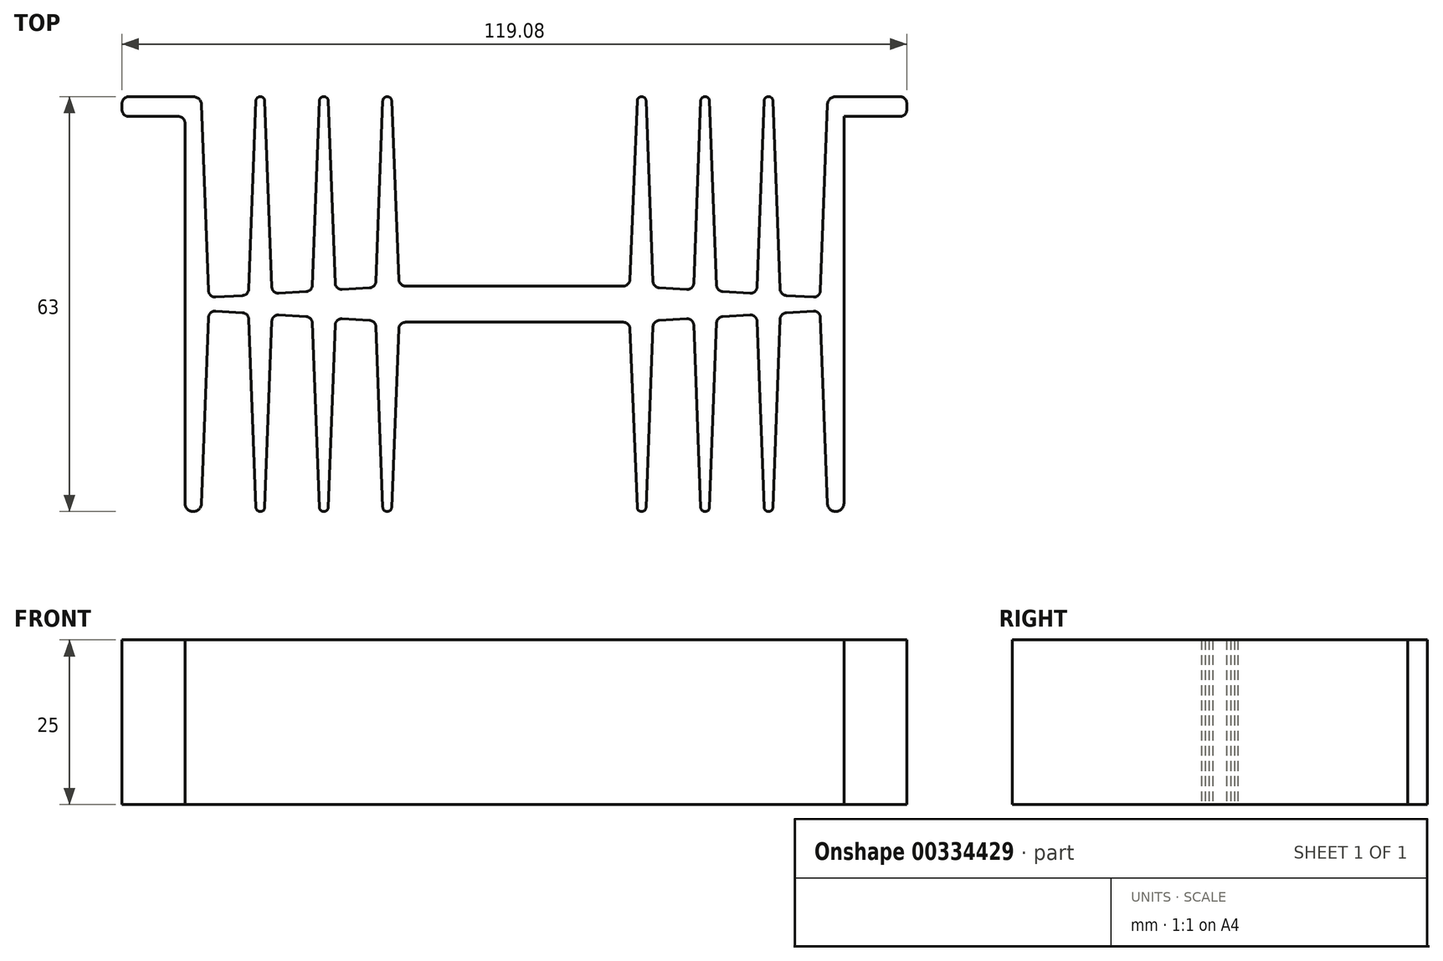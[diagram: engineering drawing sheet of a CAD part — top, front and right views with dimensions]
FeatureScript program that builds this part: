
annotation { "Feature Type Name" : "Feature", "Feature Type Description" : "" }
export const myFeature = defineFeature(function(context is Context, id is Id, definition is map)
    precondition{}
    {
        {
            var Q0;
            Q0=qCreatedBy(makeId("Top.planeOp"),FACE);
            var sketch = newSketch(context, id + "F0", { "sketchPlane" : qUnion([Q0])});
            skLineSegment(sketch, "E0.bottom", {"start": v(-50, 31.5) * mm, "end": v(50, 31.5) * mm, "construction": true});
            skLineSegment(sketch, "E0.top", {"start": v(-50, -31.5) * mm, "end": v(50, -31.5) * mm, "construction": true});
            skLineSegment(sketch, "E0.left", {"start": v(-50, 31.5) * mm, "end": v(-50, -31.5) * mm, "construction": true});
            skLineSegment(sketch, "E0.right", {"start": v(50, 31.5) * mm, "end": v(50, -31.5) * mm, "construction": true});
            skPoint(sketch, "E0.middle", {"position": v(0, 0) * mm});
            skLineSegment(sketch, "E1", {"start": v(-50, 31.5) * mm, "end": v(-47.54, 31.5) * mm});
            skLineSegment(sketch, "E2", {"start": v(-47.54, 31.5) * mm, "end": v(-46.39, 1) * mm});
            skLineSegment(sketch, "E3", {"start": v(-46.39, 1) * mm, "end": v(-40.37, 1) * mm});
            skLineSegment(sketch, "E4", {"start": v(-40.37, 1) * mm, "end": v(-39.21, 31.5) * mm});
            skLineSegment(sketch, "E5", {"start": v(-39.21, 31.5) * mm, "end": v(-37.91, 31.5) * mm});
            skLineSegment(sketch, "E6", {"start": v(-37.91, 31.5) * mm, "end": v(-36.76, 1) * mm});
            skLineSegment(sketch, "E7", {"start": v(-36.76, 1) * mm, "end": v(-30.74, 1) * mm});
            skLineSegment(sketch, "E8", {"start": v(-30.74, 1) * mm, "end": v(-29.59, 31.5) * mm});
            skLineSegment(sketch, "E9", {"start": v(-29.59, 31.5) * mm, "end": v(-28.29, 31.5) * mm});
            skLineSegment(sketch, "E10", {"start": v(-28.29, 31.5) * mm, "end": v(-27.13, 1) * mm});
            skLineSegment(sketch, "E11", {"start": v(-27.13, 1) * mm, "end": v(-21.11, 1) * mm});
            skLineSegment(sketch, "E12", {"start": v(-21.11, 1) * mm, "end": v(-19.96, 31.5) * mm});
            skLineSegment(sketch, "E13", {"start": v(-19.96, 31.5) * mm, "end": v(-18.66, 31.5) * mm});
            skLineSegment(sketch, "E14", {"start": v(-18.66, 31.5) * mm, "end": v(-17.5, 2.75) * mm});
            skLineSegment(sketch, "E15", {"start": v(-17.5, 2.75) * mm, "end": v(0, 2.75) * mm});
            skPoint(sketch, "E16", {"position": v(-43.38, 1) * mm});
            skPoint(sketch, "E17", {"position": v(-33.75, 1) * mm});
            skPoint(sketch, "E18", {"position": v(-24.12, 1) * mm});
            skLineSegment(sketch, "E19", {"start": v(-50, 0) * mm, "end": v(50, 0) * mm, "construction": true});
            skPoint(sketch, "E20", {"position": v(-8.75, 2.75) * mm});
            skLineSegment(sketch, "E21", {"start": v(-17.5, 2.75) * mm, "end": v(-46.39, 1) * mm});
            skLineSegment(sketch, "E22", {"start": v(-40.37, 1) * mm, "end": v(-36.76, 1) * mm, "construction": true});
            skLineSegment(sketch, "E23", {"start": v(-46.39, 1) * mm, "end": v(-50, 1) * mm, "construction": true});
            skLineSegment(sketch, "E24", {"start": v(-30.74, 1) * mm, "end": v(-27.13, 1) * mm, "construction": true});
            skLineSegment(sketch, "E25", {"start": v(-17.5, 2.75) * mm, "end": v(-17.5, 1) * mm, "construction": true});
            skLineSegment(sketch, "E26", {"start": v(-17.5, 1) * mm, "end": v(-21.11, 1) * mm, "construction": true});
            skPoint(sketch, "E27", {"position": v(-38.56, 31.5) * mm});
            skPoint(sketch, "E28", {"position": v(-38.56, 1) * mm});
            skPoint(sketch, "E29", {"position": v(-28.94, 31.5) * mm});
            skPoint(sketch, "E30", {"position": v(-28.94, 1) * mm});
            skPoint(sketch, "E31", {"position": v(-19.3, 31.5) * mm});
            skPoint(sketch, "E32", {"position": v(-19.3, 1) * mm});
            skLineSegment(sketch, "E33", {"start": v(-50, 31.5) * mm, "end": v(-50, 0) * mm});
            skLineSegment(sketch, "E34.MirrorCS", {"start": v(19.96, 31.5) * mm, "end": v(18.66, 31.5) * mm});
            skLineSegment(sketch, "E35.MirrorCS", {"start": v(29.59, 31.5) * mm, "end": v(28.29, 31.5) * mm});
            skLineSegment(sketch, "E36.MirrorCS", {"start": v(39.21, 31.5) * mm, "end": v(37.91, 31.5) * mm});
            skLineSegment(sketch, "E37.MirrorCS", {"start": v(17.5, 2.75) * mm, "end": v(17.5, 1) * mm, "construction": true});
            skLineSegment(sketch, "E38.MirrorCS", {"start": v(50, 31.5) * mm, "end": v(47.54, 31.5) * mm});
            skLineSegment(sketch, "E39.MirrorCS", {"start": v(17.5, 1) * mm, "end": v(21.11, 1) * mm, "construction": true});
            skLineSegment(sketch, "E40.MirrorCS", {"start": v(30.74, 1) * mm, "end": v(27.13, 1) * mm, "construction": true});
            skLineSegment(sketch, "E41.MirrorCS", {"start": v(36.76, 1) * mm, "end": v(30.74, 1) * mm});
            skLineSegment(sketch, "E42.MirrorCS", {"start": v(46.39, 1) * mm, "end": v(40.37, 1) * mm});
            skLineSegment(sketch, "E43.MirrorCS", {"start": v(46.39, 1) * mm, "end": v(50, 1) * mm, "construction": true});
            skLineSegment(sketch, "E44.MirrorCS", {"start": v(40.37, 1) * mm, "end": v(36.76, 1) * mm, "construction": true});
            skLineSegment(sketch, "E45.MirrorCS", {"start": v(27.13, 1) * mm, "end": v(21.11, 1) * mm});
            skLineSegment(sketch, "E46.MirrorCS", {"start": v(50, 31.5) * mm, "end": v(50, 0) * mm});
            skPoint(sketch, "E47.MirrorP", {"position": v(33.75, 1) * mm});
            skLineSegment(sketch, "E48.MirrorCS", {"start": v(40.37, 1) * mm, "end": v(39.21, 31.5) * mm});
            skLineSegment(sketch, "E49.MirrorCS", {"start": v(18.66, 31.5) * mm, "end": v(17.5, 2.75) * mm});
            skLineSegment(sketch, "E50.MirrorCS", {"start": v(17.5, 2.75) * mm, "end": v(0, 2.75) * mm});
            skPoint(sketch, "E51.MirrorP", {"position": v(38.56, 31.5) * mm});
            skPoint(sketch, "E52.MirrorP", {"position": v(19.3, 31.5) * mm});
            skPoint(sketch, "E53.MirrorP", {"position": v(43.38, 1) * mm});
            skPoint(sketch, "E54.MirrorP", {"position": v(28.94, 1) * mm});
            skPoint(sketch, "E55.MirrorP", {"position": v(24.12, 1) * mm});
            skLineSegment(sketch, "E56.MirrorCS", {"start": v(28.29, 31.5) * mm, "end": v(27.13, 1) * mm});
            skPoint(sketch, "E57.MirrorP", {"position": v(28.94, 31.5) * mm});
            skLineSegment(sketch, "E58.MirrorCS", {"start": v(21.11, 1) * mm, "end": v(19.96, 31.5) * mm});
            skPoint(sketch, "E59.MirrorP", {"position": v(8.75, 2.75) * mm});
            skLineSegment(sketch, "E60.MirrorCS", {"start": v(47.54, 31.5) * mm, "end": v(46.39, 1) * mm});
            skLineSegment(sketch, "E61.MirrorCS", {"start": v(37.91, 31.5) * mm, "end": v(36.76, 1) * mm});
            skLineSegment(sketch, "E62.MirrorCS", {"start": v(30.74, 1) * mm, "end": v(29.59, 31.5) * mm});
            skPoint(sketch, "E63.MirrorP", {"position": v(38.56, 1) * mm});
            skPoint(sketch, "E64.MirrorP", {"position": v(19.3, 1) * mm});
            skLineSegment(sketch, "E65.MirrorCS", {"start": v(17.5, 2.75) * mm, "end": v(46.39, 1) * mm});
            skLineSegment(sketch, "E66.MirrorCS", {"start": v(-17.5, -2.75) * mm, "end": v(-17.5, -1) * mm, "construction": true});
            skLineSegment(sketch, "E67.MirrorCS", {"start": v(17.5, -2.75) * mm, "end": v(17.5, -1) * mm, "construction": true});
            skLineSegment(sketch, "E68.MirrorCS", {"start": v(40.37, -1) * mm, "end": v(36.76, -1) * mm, "construction": true});
            skLineSegment(sketch, "E69.MirrorCS", {"start": v(-39.21, -31.5) * mm, "end": v(-37.91, -31.5) * mm});
            skLineSegment(sketch, "E70.MirrorCS", {"start": v(-29.59, -31.5) * mm, "end": v(-28.29, -31.5) * mm});
            skLineSegment(sketch, "E71.MirrorCS", {"start": v(39.21, -31.5) * mm, "end": v(37.91, -31.5) * mm});
            skLineSegment(sketch, "E72.MirrorCS", {"start": v(29.59, -31.5) * mm, "end": v(28.29, -31.5) * mm});
            skLineSegment(sketch, "E73.MirrorCS", {"start": v(-19.96, -31.5) * mm, "end": v(-18.66, -31.5) * mm});
            skLineSegment(sketch, "E74.MirrorCS", {"start": v(19.96, -31.5) * mm, "end": v(18.66, -31.5) * mm});
            skLineSegment(sketch, "E75.MirrorCS", {"start": v(50, -31.5) * mm, "end": v(47.54, -31.5) * mm});
            skLineSegment(sketch, "E76.MirrorCS", {"start": v(-46.39, -1) * mm, "end": v(-50, -1) * mm, "construction": true});
            skLineSegment(sketch, "E77.MirrorCS", {"start": v(46.39, -1) * mm, "end": v(50, -1) * mm, "construction": true});
            skLineSegment(sketch, "E78.MirrorCS", {"start": v(-50, -31.5) * mm, "end": v(-47.54, -31.5) * mm});
            skLineSegment(sketch, "E79.MirrorCS", {"start": v(36.76, -1) * mm, "end": v(30.74, -1) * mm});
            skLineSegment(sketch, "E80.MirrorCS", {"start": v(27.13, -1) * mm, "end": v(21.11, -1) * mm});
            skLineSegment(sketch, "E81.MirrorCS", {"start": v(-17.5, -1) * mm, "end": v(-21.11, -1) * mm, "construction": true});
            skLineSegment(sketch, "E82.MirrorCS", {"start": v(-40.37, -1) * mm, "end": v(-36.76, -1) * mm, "construction": true});
            skLineSegment(sketch, "E83.MirrorCS", {"start": v(-36.76, -1) * mm, "end": v(-30.74, -1) * mm});
            skLineSegment(sketch, "E84.MirrorCS", {"start": v(17.5, -2.75) * mm, "end": v(46.39, -1) * mm});
            skLineSegment(sketch, "E85.MirrorCS", {"start": v(-46.39, -1) * mm, "end": v(-40.37, -1) * mm});
            skLineSegment(sketch, "E86.MirrorCS", {"start": v(46.39, -1) * mm, "end": v(40.37, -1) * mm});
            skLineSegment(sketch, "E87.MirrorCS", {"start": v(30.74, -1) * mm, "end": v(27.13, -1) * mm, "construction": true});
            skLineSegment(sketch, "E88.MirrorCS", {"start": v(17.5, -1) * mm, "end": v(21.11, -1) * mm, "construction": true});
            skLineSegment(sketch, "E89.MirrorCS", {"start": v(-30.74, -1) * mm, "end": v(-27.13, -1) * mm, "construction": true});
            skLineSegment(sketch, "E90.MirrorCS", {"start": v(-27.13, -1) * mm, "end": v(-21.11, -1) * mm});
            skLineSegment(sketch, "E91.MirrorCS", {"start": v(-17.5, -2.75) * mm, "end": v(-46.39, -1) * mm});
            skPoint(sketch, "E92.MirrorP", {"position": v(-28.94, -31.5) * mm});
            skLineSegment(sketch, "E93.MirrorCS", {"start": v(-17.5, -2.75) * mm, "end": v(0, -2.75) * mm});
            skLineSegment(sketch, "E94.MirrorCS", {"start": v(30.74, -1) * mm, "end": v(29.59, -31.5) * mm});
            skLineSegment(sketch, "E95.MirrorCS", {"start": v(18.66, -31.5) * mm, "end": v(17.5, -2.75) * mm});
            skPoint(sketch, "E96.MirrorP", {"position": v(24.12, -1) * mm});
            skLineSegment(sketch, "E97.MirrorCS", {"start": v(-50, -31.5) * mm, "end": v(-50, 0) * mm});
            skLineSegment(sketch, "E98.MirrorCS", {"start": v(-18.66, -31.5) * mm, "end": v(-17.5, -2.75) * mm});
            skPoint(sketch, "E99.MirrorP", {"position": v(8.75, -2.75) * mm});
            skPoint(sketch, "E100.MirrorP", {"position": v(28.94, -1) * mm});
            skLineSegment(sketch, "E101.MirrorCS", {"start": v(-28.29, -31.5) * mm, "end": v(-27.13, -1) * mm});
            skPoint(sketch, "E102.MirrorP", {"position": v(-43.38, -1) * mm});
            skPoint(sketch, "E103.MirrorP", {"position": v(-33.75, -1) * mm});
            skLineSegment(sketch, "E104.MirrorCS", {"start": v(50, -31.5) * mm, "end": v(50, 0) * mm});
            skLineSegment(sketch, "E105.MirrorCS", {"start": v(21.11, -1) * mm, "end": v(19.96, -31.5) * mm});
            skPoint(sketch, "E106.MirrorP", {"position": v(-38.56, -31.5) * mm});
            skLineSegment(sketch, "E107.MirrorCS", {"start": v(-37.91, -31.5) * mm, "end": v(-36.76, -1) * mm});
            skLineSegment(sketch, "E108.MirrorCS", {"start": v(17.5, -2.75) * mm, "end": v(0, -2.75) * mm});
            skPoint(sketch, "E109.MirrorP", {"position": v(43.38, -1) * mm});
            skLineSegment(sketch, "E110.MirrorCS", {"start": v(28.29, -31.5) * mm, "end": v(27.13, -1) * mm});
            skLineSegment(sketch, "E111.MirrorCS", {"start": v(40.37, -1) * mm, "end": v(39.21, -31.5) * mm});
            skLineSegment(sketch, "E112.MirrorCS", {"start": v(-40.37, -1) * mm, "end": v(-39.21, -31.5) * mm});
            skPoint(sketch, "E113.MirrorP", {"position": v(19.3, -1) * mm});
            skLineSegment(sketch, "E114.MirrorCS", {"start": v(47.54, -31.5) * mm, "end": v(46.39, -1) * mm});
            skPoint(sketch, "E115.MirrorP", {"position": v(-19.3, -1) * mm});
            skLineSegment(sketch, "E116.MirrorCS", {"start": v(-30.74, -1) * mm, "end": v(-29.59, -31.5) * mm});
            skPoint(sketch, "E117.MirrorP", {"position": v(19.3, -31.5) * mm});
            skPoint(sketch, "E118.MirrorP", {"position": v(38.56, -1) * mm});
            skLineSegment(sketch, "E119.MirrorCS", {"start": v(37.91, -31.5) * mm, "end": v(36.76, -1) * mm});
            skPoint(sketch, "E120.MirrorP", {"position": v(-8.75, -2.75) * mm});
            skLineSegment(sketch, "E121.MirrorCS", {"start": v(-47.54, -31.5) * mm, "end": v(-46.39, -1) * mm});
            skPoint(sketch, "E122.MirrorP", {"position": v(28.94, -31.5) * mm});
            skPoint(sketch, "E123.MirrorP", {"position": v(38.56, -31.5) * mm});
            skPoint(sketch, "E124.MirrorP", {"position": v(-28.94, -1) * mm});
            skPoint(sketch, "E125.MirrorP", {"position": v(-38.56, -1) * mm});
            skPoint(sketch, "E126.MirrorP", {"position": v(-19.3, -31.5) * mm});
            skPoint(sketch, "E127.MirrorP", {"position": v(33.75, -1) * mm});
            skLineSegment(sketch, "E128.MirrorCS", {"start": v(-21.11, -1) * mm, "end": v(-19.96, -31.5) * mm});
            skPoint(sketch, "E129.MirrorP", {"position": v(-24.12, -1) * mm});
            skLineSegment(sketch, "E130.bottom", {"start": v(-47.54, 31.5) * mm, "end": v(-59.54, 31.5) * mm});
            skLineSegment(sketch, "E130.top", {"start": v(-47.54, 28.5) * mm, "end": v(-59.54, 28.5) * mm});
            skLineSegment(sketch, "E130.left", {"start": v(-47.54, 31.5) * mm, "end": v(-47.54, 28.5) * mm});
            skLineSegment(sketch, "E130.right", {"start": v(-59.54, 31.5) * mm, "end": v(-59.54, 28.5) * mm});
            skLineSegment(sketch, "E131.bottom", {"start": v(47.54, 31.5) * mm, "end": v(59.54, 31.5) * mm});
            skLineSegment(sketch, "E131.top", {"start": v(47.54, 28.5) * mm, "end": v(59.54, 28.5) * mm});
            skLineSegment(sketch, "E131.left", {"start": v(47.54, 31.5) * mm, "end": v(47.54, 28.5) * mm});
            skLineSegment(sketch, "E131.right", {"start": v(59.54, 31.5) * mm, "end": v(59.54, 28.5) * mm});
            skSolve(sketch);
        }
        {
            var Q0;
            {var subQ5=sQuery(id+"F0.wireOp",EDGE,"E130.right");Q0=makeQuery(id+"F0.imprint","IMPRINT",FACE,{"disambiguationData":[TD([[makeQuery(id+"F0.imprint","IMPRINT",EDGE,{"derivedFrom":subQ5}),1.0]])]});}
            var Q1;
            {var subQ5=sQuery(id+"F0.wireOp",EDGE,"E130.left");Q1=makeQuery(id+"F0.imprint","IMPRINT",FACE,{"disambiguationData":[TD([[makeQuery(id+"F0.imprint","IMPRINT",EDGE,{"derivedFrom":subQ5}),-1.0]])]});}
            var Q2;
            Q2=makeQuery(id+"F0.imprint","IMPRINT",FACE,{"disambiguationData":[TD([[makeQuery(id+"F0.imprint","IMPRINT",EDGE,{"derivedFrom":sQuery(id+"F0.wireOp",EDGE,"E2")}),-1.0]])]});
            var Q3;
            {var subQ0=sQuery(id+"F0.wireOp",EDGE,"E69.MirrorCS");Q3=makeQuery(id+"F0.imprint","IMPRINT",FACE,{"disambiguationData":[TD([[makeQuery(id+"F0.imprint","IMPRINT",EDGE,{"derivedFrom":subQ0}),1.0]])]});}
            var Q4;
            {var subQ0=sQuery(id+"F0.wireOp",EDGE,"E5");Q4=makeQuery(id+"F0.imprint","IMPRINT",FACE,{"disambiguationData":[TD([[makeQuery(id+"F0.imprint","IMPRINT",EDGE,{"derivedFrom":subQ0}),-1.0]])]});}
            var Q5;
            {var subQ0=sQuery(id+"F0.wireOp",EDGE,"E70.MirrorCS");Q5=makeQuery(id+"F0.imprint","IMPRINT",FACE,{"disambiguationData":[TD([[makeQuery(id+"F0.imprint","IMPRINT",EDGE,{"derivedFrom":subQ0}),1.0]])]});}
            var Q6;
            {var subQ0=sQuery(id+"F0.wireOp",EDGE,"E9");Q6=makeQuery(id+"F0.imprint","IMPRINT",FACE,{"disambiguationData":[TD([[makeQuery(id+"F0.imprint","IMPRINT",EDGE,{"derivedFrom":subQ0}),-1.0]])]});}
            var Q7;
            {var subQ0=sQuery(id+"F0.wireOp",EDGE,"E73.MirrorCS");Q7=makeQuery(id+"F0.imprint","IMPRINT",FACE,{"disambiguationData":[TD([[makeQuery(id+"F0.imprint","IMPRINT",EDGE,{"derivedFrom":subQ0}),1.0]])]});}
            var Q8;
            {var subQ0=sQuery(id+"F0.wireOp",EDGE,"E13");Q8=makeQuery(id+"F0.imprint","IMPRINT",FACE,{"disambiguationData":[TD([[makeQuery(id+"F0.imprint","IMPRINT",EDGE,{"derivedFrom":subQ0}),-1.0]])]});}
            var Q9;
            {var subQ0=sQuery(id+"F0.wireOp",EDGE,"E74.MirrorCS");Q9=makeQuery(id+"F0.imprint","IMPRINT",FACE,{"disambiguationData":[TD([[makeQuery(id+"F0.imprint","IMPRINT",EDGE,{"derivedFrom":subQ0}),-1.0]])]});}
            var Q10;
            {var subQ0=sQuery(id+"F0.wireOp",EDGE,"E34.MirrorCS");Q10=makeQuery(id+"F0.imprint","IMPRINT",FACE,{"disambiguationData":[TD([[makeQuery(id+"F0.imprint","IMPRINT",EDGE,{"derivedFrom":subQ0}),1.0]])]});}
            var Q11;
            {var subQ0=sQuery(id+"F0.wireOp",EDGE,"E35.MirrorCS");Q11=makeQuery(id+"F0.imprint","IMPRINT",FACE,{"disambiguationData":[TD([[makeQuery(id+"F0.imprint","IMPRINT",EDGE,{"derivedFrom":subQ0}),1.0]])]});}
            var Q12;
            {var subQ0=sQuery(id+"F0.wireOp",EDGE,"E72.MirrorCS");Q12=makeQuery(id+"F0.imprint","IMPRINT",FACE,{"disambiguationData":[TD([[makeQuery(id+"F0.imprint","IMPRINT",EDGE,{"derivedFrom":subQ0}),-1.0]])]});}
            var Q13;
            {var subQ0=sQuery(id+"F0.wireOp",EDGE,"E71.MirrorCS");Q13=makeQuery(id+"F0.imprint","IMPRINT",FACE,{"disambiguationData":[TD([[makeQuery(id+"F0.imprint","IMPRINT",EDGE,{"derivedFrom":subQ0}),-1.0]])]});}
            var Q14;
            {var subQ0=sQuery(id+"F0.wireOp",EDGE,"E36.MirrorCS");Q14=makeQuery(id+"F0.imprint","IMPRINT",FACE,{"disambiguationData":[TD([[makeQuery(id+"F0.imprint","IMPRINT",EDGE,{"derivedFrom":subQ0}),1.0]])]});}
            var Q15;
            {var subQ5=sQuery(id+"F0.wireOp",EDGE,"E131.right");Q15=makeQuery(id+"F0.imprint","IMPRINT",FACE,{"disambiguationData":[TD([[makeQuery(id+"F0.imprint","IMPRINT",EDGE,{"derivedFrom":subQ5}),-1.0]])]});}
            var Q16;
            {var subQ5=sQuery(id+"F0.wireOp",EDGE,"E131.left");Q16=makeQuery(id+"F0.imprint","IMPRINT",FACE,{"disambiguationData":[TD([[makeQuery(id+"F0.imprint","IMPRINT",EDGE,{"derivedFrom":subQ5}),1.0]])]});}
            var Q17;
            {var subQ0=sQuery(id+"F0.wireOp",EDGE,"E83.MirrorCS");Q17=makeQuery(id+"F0.imprint","IMPRINT",FACE,{"disambiguationData":[TD([[makeQuery(id+"F0.imprint","IMPRINT",EDGE,{"derivedFrom":subQ0}),-1.0]])]});}
            var Q18;
            {var subQ0=sQuery(id+"F0.wireOp",EDGE,"E90.MirrorCS");Q18=makeQuery(id+"F0.imprint","IMPRINT",FACE,{"disambiguationData":[TD([[makeQuery(id+"F0.imprint","IMPRINT",EDGE,{"derivedFrom":subQ0}),-1.0]])]});}
            var Q19;
            {var subQ0=sQuery(id+"F0.wireOp",EDGE,"E11");Q19=makeQuery(id+"F0.imprint","IMPRINT",FACE,{"disambiguationData":[TD([[makeQuery(id+"F0.imprint","IMPRINT",EDGE,{"derivedFrom":subQ0}),1.0]])]});}
            var Q20;
            {var subQ0=sQuery(id+"F0.wireOp",EDGE,"E7");Q20=makeQuery(id+"F0.imprint","IMPRINT",FACE,{"disambiguationData":[TD([[makeQuery(id+"F0.imprint","IMPRINT",EDGE,{"derivedFrom":subQ0}),1.0]])]});}
            var Q21;
            {var subQ0=sQuery(id+"F0.wireOp",EDGE,"E3");Q21=makeQuery(id+"F0.imprint","IMPRINT",FACE,{"disambiguationData":[TD([[makeQuery(id+"F0.imprint","IMPRINT",EDGE,{"derivedFrom":subQ0}),1.0]])]});}
            var Q22;
            {var subQ0=sQuery(id+"F0.wireOp",EDGE,"E85.MirrorCS");Q22=makeQuery(id+"F0.imprint","IMPRINT",FACE,{"disambiguationData":[TD([[makeQuery(id+"F0.imprint","IMPRINT",EDGE,{"derivedFrom":subQ0}),-1.0]])]});}
            var Q23;
            {var subQ0=sQuery(id+"F0.wireOp",EDGE,"E80.MirrorCS");Q23=makeQuery(id+"F0.imprint","IMPRINT",FACE,{"disambiguationData":[TD([[makeQuery(id+"F0.imprint","IMPRINT",EDGE,{"derivedFrom":subQ0}),1.0]])]});}
            var Q24;
            {var subQ0=sQuery(id+"F0.wireOp",EDGE,"E45.MirrorCS");Q24=makeQuery(id+"F0.imprint","IMPRINT",FACE,{"disambiguationData":[TD([[makeQuery(id+"F0.imprint","IMPRINT",EDGE,{"derivedFrom":subQ0}),-1.0]])]});}
            var Q25;
            {var subQ0=sQuery(id+"F0.wireOp",EDGE,"E41.MirrorCS");Q25=makeQuery(id+"F0.imprint","IMPRINT",FACE,{"disambiguationData":[TD([[makeQuery(id+"F0.imprint","IMPRINT",EDGE,{"derivedFrom":subQ0}),-1.0]])]});}
            var Q26;
            {var subQ0=sQuery(id+"F0.wireOp",EDGE,"E79.MirrorCS");Q26=makeQuery(id+"F0.imprint","IMPRINT",FACE,{"disambiguationData":[TD([[makeQuery(id+"F0.imprint","IMPRINT",EDGE,{"derivedFrom":subQ0}),1.0]])]});}
            var Q27;
            {var subQ0=sQuery(id+"F0.wireOp",EDGE,"E86.MirrorCS");Q27=makeQuery(id+"F0.imprint","IMPRINT",FACE,{"disambiguationData":[TD([[makeQuery(id+"F0.imprint","IMPRINT",EDGE,{"derivedFrom":subQ0}),1.0]])]});}
            var Q28;
            {var subQ0=sQuery(id+"F0.wireOp",EDGE,"E42.MirrorCS");Q28=makeQuery(id+"F0.imprint","IMPRINT",FACE,{"disambiguationData":[TD([[makeQuery(id+"F0.imprint","IMPRINT",EDGE,{"derivedFrom":subQ0}),-1.0]])]});}
            extrude(context, id + "F1", {"entities" : qUnion([Q0, Q1, Q2, Q3, Q4, Q5, Q6, Q7, Q8, Q9, Q10, Q11, Q12, Q13, Q14, Q15, Q16, Q17, Q18, Q19, Q20, Q21, Q22, Q23, Q24, Q25, Q26, Q27, Q28]), "offsetDistance" : 25 * mm, "depth" : 25 * mm});
        }
        {
            var Q0;
            Q0=makeQuery(id+"F1.opExtrude","SWEPT_EDGE",EDGE,{"disambiguationData":[OSD([sQuery(id+"F0.wireOp",EDGE,"E35.MirrorCS"),sQuery(id+"F0.wireOp",EDGE,"E62.MirrorCS")])]});
            var Q1;
            Q1=makeQuery(id+"F1.opExtrude","SWEPT_EDGE",EDGE,{"disambiguationData":[OSD([sQuery(id+"F0.wireOp",EDGE,"E35.MirrorCS"),sQuery(id+"F0.wireOp",EDGE,"E56.MirrorCS")])]});
            var Q2;
            Q2=makeQuery(id+"F1.opExtrude","SWEPT_EDGE",EDGE,{"disambiguationData":[OSD([sQuery(id+"F0.wireOp",EDGE,"E36.MirrorCS"),sQuery(id+"F0.wireOp",EDGE,"E48.MirrorCS")])]});
            var Q3;
            Q3=makeQuery(id+"F1.opExtrude","SWEPT_EDGE",EDGE,{"disambiguationData":[OSD([sQuery(id+"F0.wireOp",EDGE,"E36.MirrorCS"),sQuery(id+"F0.wireOp",EDGE,"E61.MirrorCS")])]});
            var Q4;
            Q4=makeQuery(id+"F1.opExtrude","SWEPT_EDGE",EDGE,{"disambiguationData":[OSD([sQuery(id+"F0.wireOp",EDGE,"E34.MirrorCS"),sQuery(id+"F0.wireOp",EDGE,"E58.MirrorCS")])]});
            var Q5;
            Q5=makeQuery(id+"F1.opExtrude","SWEPT_EDGE",EDGE,{"disambiguationData":[OSD([sQuery(id+"F0.wireOp",EDGE,"E34.MirrorCS"),sQuery(id+"F0.wireOp",EDGE,"E49.MirrorCS")])]});
            var Q6;
            Q6=makeQuery(id+"F1.opExtrude","SWEPT_EDGE",EDGE,{"disambiguationData":[OSD([sQuery(id+"F0.wireOp",EDGE,"E13"),sQuery(id+"F0.wireOp",EDGE,"E14")])]});
            var Q7;
            Q7=makeQuery(id+"F1.opExtrude","SWEPT_EDGE",EDGE,{"disambiguationData":[OSD([sQuery(id+"F0.wireOp",EDGE,"E12"),sQuery(id+"F0.wireOp",EDGE,"E13")])]});
            var Q8;
            Q8=makeQuery(id+"F1.opExtrude","SWEPT_EDGE",EDGE,{"disambiguationData":[OSD([sQuery(id+"F0.wireOp",EDGE,"E9"),sQuery(id+"F0.wireOp",EDGE,"E10")])]});
            var Q9;
            Q9=makeQuery(id+"F1.opExtrude","SWEPT_EDGE",EDGE,{"disambiguationData":[OSD([sQuery(id+"F0.wireOp",EDGE,"E8"),sQuery(id+"F0.wireOp",EDGE,"E9")])]});
            var Q10;
            Q10=makeQuery(id+"F1.opExtrude","SWEPT_EDGE",EDGE,{"disambiguationData":[OSD([sQuery(id+"F0.wireOp",EDGE,"E5"),sQuery(id+"F0.wireOp",EDGE,"E6")])]});
            var Q11;
            Q11=makeQuery(id+"F1.opExtrude","SWEPT_EDGE",EDGE,{"disambiguationData":[OSD([sQuery(id+"F0.wireOp",EDGE,"E4"),sQuery(id+"F0.wireOp",EDGE,"E5")])]});
            var Q12;
            Q12=makeQuery(id+"F1.opExtrude","SWEPT_EDGE",EDGE,{"disambiguationData":[OSD([sQuery(id+"F0.wireOp",EDGE,"E69.MirrorCS"),sQuery(id+"F0.wireOp",EDGE,"E112.MirrorCS")])]});
            var Q13;
            Q13=makeQuery(id+"F1.opExtrude","SWEPT_EDGE",EDGE,{"disambiguationData":[OSD([sQuery(id+"F0.wireOp",EDGE,"E69.MirrorCS"),sQuery(id+"F0.wireOp",EDGE,"E107.MirrorCS")])]});
            var Q14;
            Q14=makeQuery(id+"F1.opExtrude","SWEPT_EDGE",EDGE,{"disambiguationData":[OSD([sQuery(id+"F0.wireOp",EDGE,"E70.MirrorCS"),sQuery(id+"F0.wireOp",EDGE,"E116.MirrorCS")])]});
            var Q15;
            Q15=makeQuery(id+"F1.opExtrude","SWEPT_EDGE",EDGE,{"disambiguationData":[OSD([sQuery(id+"F0.wireOp",EDGE,"E70.MirrorCS"),sQuery(id+"F0.wireOp",EDGE,"E101.MirrorCS")])]});
            var Q16;
            Q16=makeQuery(id+"F1.opExtrude","SWEPT_EDGE",EDGE,{"disambiguationData":[OSD([sQuery(id+"F0.wireOp",EDGE,"E73.MirrorCS"),sQuery(id+"F0.wireOp",EDGE,"E128.MirrorCS")])]});
            var Q17;
            Q17=makeQuery(id+"F1.opExtrude","SWEPT_EDGE",EDGE,{"disambiguationData":[OSD([sQuery(id+"F0.wireOp",EDGE,"E73.MirrorCS"),sQuery(id+"F0.wireOp",EDGE,"E98.MirrorCS")])]});
            var Q18;
            Q18=makeQuery(id+"F1.opExtrude","SWEPT_EDGE",EDGE,{"disambiguationData":[OSD([sQuery(id+"F0.wireOp",EDGE,"E74.MirrorCS"),sQuery(id+"F0.wireOp",EDGE,"E95.MirrorCS")])]});
            var Q19;
            Q19=makeQuery(id+"F1.opExtrude","SWEPT_EDGE",EDGE,{"disambiguationData":[OSD([sQuery(id+"F0.wireOp",EDGE,"E74.MirrorCS"),sQuery(id+"F0.wireOp",EDGE,"E105.MirrorCS")])]});
            var Q20;
            Q20=makeQuery(id+"F1.opExtrude","SWEPT_EDGE",EDGE,{"disambiguationData":[OSD([sQuery(id+"F0.wireOp",EDGE,"E72.MirrorCS"),sQuery(id+"F0.wireOp",EDGE,"E110.MirrorCS")])]});
            var Q21;
            Q21=makeQuery(id+"F1.opExtrude","SWEPT_EDGE",EDGE,{"disambiguationData":[OSD([sQuery(id+"F0.wireOp",EDGE,"E72.MirrorCS"),sQuery(id+"F0.wireOp",EDGE,"E94.MirrorCS")])]});
            var Q22;
            Q22=makeQuery(id+"F1.opExtrude","SWEPT_EDGE",EDGE,{"disambiguationData":[OSD([sQuery(id+"F0.wireOp",EDGE,"E71.MirrorCS"),sQuery(id+"F0.wireOp",EDGE,"E119.MirrorCS")])]});
            var Q23;
            Q23=makeQuery(id+"F1.opExtrude","SWEPT_EDGE",EDGE,{"disambiguationData":[OSD([sQuery(id+"F0.wireOp",EDGE,"E71.MirrorCS"),sQuery(id+"F0.wireOp",EDGE,"E111.MirrorCS")])]});
            fillet(context, id + "F2", {"entities" : qUnion([Q0, Q1, Q2, Q3, Q4, Q5, Q6, Q7, Q8, Q9, Q10, Q11, Q12, Q13, Q14, Q15, Q16, Q17, Q18, Q19, Q20, Q21, Q22, Q23]), "radius" : (1.3 / 2) * mm, "tangentPropagation" : true, "allowEdgeOverflow" : false});
        }
        {
            var Q0;
            Q0=makeQuery(id+"F1.opExtrude","SWEPT_EDGE",EDGE,{"disambiguationData":[OSD([sQuery(id+"F0.wireOp",EDGE,"E78.MirrorCS"),sQuery(id+"F0.wireOp",EDGE,"E97.MirrorCS")])]});
            var Q1;
            Q1=makeQuery(id+"F1.opExtrude","SWEPT_EDGE",EDGE,{"disambiguationData":[OSD([sQuery(id+"F0.wireOp",EDGE,"E78.MirrorCS"),sQuery(id+"F0.wireOp",EDGE,"E121.MirrorCS")])]});
            var Q2;
            Q2=makeQuery(id+"F1.opExtrude","SWEPT_EDGE",EDGE,{"disambiguationData":[OSD([sQuery(id+"F0.wireOp",EDGE,"E75.MirrorCS"),sQuery(id+"F0.wireOp",EDGE,"E114.MirrorCS")])]});
            var Q3;
            Q3=makeQuery(id+"F1.opExtrude","SWEPT_EDGE",EDGE,{"disambiguationData":[OSD([sQuery(id+"F0.wireOp",EDGE,"E75.MirrorCS"),sQuery(id+"F0.wireOp",EDGE,"E104.MirrorCS")])]});
            var Q4;
            Q4=makeQuery(id+"F1.opExtrude","SWEPT_EDGE",EDGE,{"disambiguationData":[OSD([sQuery(id+"F0.wireOp",EDGE,"E2"),sQuery(id+"F0.wireOp",EDGE,"E130.bottom"),sQuery(id+"F0.wireOp",EDGE,"E130.left")])]});
            var Q5;
            Q5=makeQuery(id+"F1.opExtrude","SWEPT_EDGE",EDGE,{"disambiguationData":[OSD([sQuery(id+"F0.wireOp",EDGE,"E60.MirrorCS"),sQuery(id+"F0.wireOp",EDGE,"E131.bottom"),sQuery(id+"F0.wireOp",EDGE,"E131.left")])]});
            fillet(context, id + "F3", {"entities" : qUnion([Q0, Q1, Q2, Q3, Q4, Q5]), "radius" : 2.46 / 2 * mm, "tangentPropagation" : true, "allowEdgeOverflow" : false});
        }
        {
            var Q0;
            Q0=makeQuery(id+"F1.opExtrude","SWEPT_EDGE",EDGE,{"disambiguationData":[OSD([sQuery(id+"F0.wireOp",EDGE,"E33"),sQuery(id+"F0.wireOp",EDGE,"E130.top")])]});
            var Q1;
            Q1=makeQuery(id+"F1.opExtrude","SWEPT_EDGE",EDGE,{"disambiguationData":[OSD([sQuery(id+"F0.wireOp",EDGE,"E4"),sQuery(id+"F0.wireOp",EDGE,"E21")])]});
            var Q2;
            Q2=makeQuery(id+"F1.opExtrude","SWEPT_EDGE",EDGE,{"disambiguationData":[OSD([sQuery(id+"F0.wireOp",EDGE,"E2"),sQuery(id+"F0.wireOp",EDGE,"E3"),sQuery(id+"F0.wireOp",EDGE,"E21")])]});
            var Q3;
            Q3=makeQuery(id+"F1.opExtrude","SWEPT_EDGE",EDGE,{"disambiguationData":[OSD([sQuery(id+"F0.wireOp",EDGE,"E6"),sQuery(id+"F0.wireOp",EDGE,"E21")])]});
            var Q4;
            Q4=makeQuery(id+"F1.opExtrude","SWEPT_EDGE",EDGE,{"disambiguationData":[OSD([sQuery(id+"F0.wireOp",EDGE,"E8"),sQuery(id+"F0.wireOp",EDGE,"E21")])]});
            var Q5;
            Q5=makeQuery(id+"F1.opExtrude","SWEPT_EDGE",EDGE,{"disambiguationData":[OSD([sQuery(id+"F0.wireOp",EDGE,"E12"),sQuery(id+"F0.wireOp",EDGE,"E21")])]});
            var Q6;
            Q6=makeQuery(id+"F1.opExtrude","SWEPT_EDGE",EDGE,{"disambiguationData":[OSD([sQuery(id+"F0.wireOp",EDGE,"E10"),sQuery(id+"F0.wireOp",EDGE,"E21")])]});
            var Q7;
            Q7=makeQuery(id+"F1.opExtrude","SWEPT_EDGE",EDGE,{"disambiguationData":[OSD([sQuery(id+"F0.wireOp",EDGE,"E91.MirrorCS"),sQuery(id+"F0.wireOp",EDGE,"E112.MirrorCS")])]});
            var Q8;
            Q8=makeQuery(id+"F1.opExtrude","SWEPT_EDGE",EDGE,{"disambiguationData":[OSD([sQuery(id+"F0.wireOp",EDGE,"E85.MirrorCS"),sQuery(id+"F0.wireOp",EDGE,"E91.MirrorCS"),sQuery(id+"F0.wireOp",EDGE,"E121.MirrorCS")])]});
            var Q9;
            Q9=makeQuery(id+"F1.opExtrude","SWEPT_EDGE",EDGE,{"disambiguationData":[OSD([sQuery(id+"F0.wireOp",EDGE,"E91.MirrorCS"),sQuery(id+"F0.wireOp",EDGE,"E116.MirrorCS")])]});
            var Q10;
            Q10=makeQuery(id+"F1.opExtrude","SWEPT_EDGE",EDGE,{"disambiguationData":[OSD([sQuery(id+"F0.wireOp",EDGE,"E91.MirrorCS"),sQuery(id+"F0.wireOp",EDGE,"E128.MirrorCS")])]});
            var Q11;
            Q11=makeQuery(id+"F1.opExtrude","SWEPT_EDGE",EDGE,{"disambiguationData":[OSD([sQuery(id+"F0.wireOp",EDGE,"E91.MirrorCS"),sQuery(id+"F0.wireOp",EDGE,"E101.MirrorCS")])]});
            var Q12;
            Q12=makeQuery(id+"F1.opExtrude","SWEPT_EDGE",EDGE,{"disambiguationData":[OSD([sQuery(id+"F0.wireOp",EDGE,"E91.MirrorCS"),sQuery(id+"F0.wireOp",EDGE,"E107.MirrorCS")])]});
            var Q13;
            Q13=makeQuery(id+"F1.opExtrude","SWEPT_EDGE",EDGE,{"disambiguationData":[OSD([sQuery(id+"F0.wireOp",EDGE,"E14"),sQuery(id+"F0.wireOp",EDGE,"E15"),sQuery(id+"F0.wireOp",EDGE,"E21")])]});
            var Q14;
            Q14=makeQuery(id+"F1.opExtrude","SWEPT_EDGE",EDGE,{"disambiguationData":[OSD([sQuery(id+"F0.wireOp",EDGE,"E91.MirrorCS"),sQuery(id+"F0.wireOp",EDGE,"E93.MirrorCS"),sQuery(id+"F0.wireOp",EDGE,"E98.MirrorCS")])]});
            var Q15;
            Q15=makeQuery(id+"F1.opExtrude","SWEPT_EDGE",EDGE,{"disambiguationData":[OSD([sQuery(id+"F0.wireOp",EDGE,"E84.MirrorCS"),sQuery(id+"F0.wireOp",EDGE,"E95.MirrorCS"),sQuery(id+"F0.wireOp",EDGE,"E108.MirrorCS")])]});
            var Q16;
            Q16=makeQuery(id+"F1.opExtrude","SWEPT_EDGE",EDGE,{"disambiguationData":[OSD([sQuery(id+"F0.wireOp",EDGE,"E49.MirrorCS"),sQuery(id+"F0.wireOp",EDGE,"E50.MirrorCS"),sQuery(id+"F0.wireOp",EDGE,"E65.MirrorCS")])]});
            var Q17;
            Q17=makeQuery(id+"F1.opExtrude","SWEPT_EDGE",EDGE,{"disambiguationData":[OSD([sQuery(id+"F0.wireOp",EDGE,"E56.MirrorCS"),sQuery(id+"F0.wireOp",EDGE,"E65.MirrorCS")])]});
            var Q18;
            Q18=makeQuery(id+"F1.opExtrude","SWEPT_EDGE",EDGE,{"disambiguationData":[OSD([sQuery(id+"F0.wireOp",EDGE,"E84.MirrorCS"),sQuery(id+"F0.wireOp",EDGE,"E110.MirrorCS")])]});
            var Q19;
            Q19=makeQuery(id+"F1.opExtrude","SWEPT_EDGE",EDGE,{"disambiguationData":[OSD([sQuery(id+"F0.wireOp",EDGE,"E84.MirrorCS"),sQuery(id+"F0.wireOp",EDGE,"E119.MirrorCS")])]});
            var Q20;
            Q20=makeQuery(id+"F1.opExtrude","SWEPT_EDGE",EDGE,{"disambiguationData":[OSD([sQuery(id+"F0.wireOp",EDGE,"E84.MirrorCS"),sQuery(id+"F0.wireOp",EDGE,"E94.MirrorCS")])]});
            var Q21;
            Q21=makeQuery(id+"F1.opExtrude","SWEPT_EDGE",EDGE,{"disambiguationData":[OSD([sQuery(id+"F0.wireOp",EDGE,"E62.MirrorCS"),sQuery(id+"F0.wireOp",EDGE,"E65.MirrorCS")])]});
            var Q22;
            Q22=makeQuery(id+"F1.opExtrude","SWEPT_EDGE",EDGE,{"disambiguationData":[OSD([sQuery(id+"F0.wireOp",EDGE,"E61.MirrorCS"),sQuery(id+"F0.wireOp",EDGE,"E65.MirrorCS")])]});
            var Q23;
            Q23=makeQuery(id+"F1.opExtrude","SWEPT_EDGE",EDGE,{"disambiguationData":[OSD([sQuery(id+"F0.wireOp",EDGE,"E84.MirrorCS"),sQuery(id+"F0.wireOp",EDGE,"E111.MirrorCS")])]});
            var Q24;
            Q24=makeQuery(id+"F1.opExtrude","SWEPT_EDGE",EDGE,{"disambiguationData":[OSD([sQuery(id+"F0.wireOp",EDGE,"E48.MirrorCS"),sQuery(id+"F0.wireOp",EDGE,"E65.MirrorCS")])]});
            var Q25;
            Q25=makeQuery(id+"F1.opExtrude","SWEPT_EDGE",EDGE,{"disambiguationData":[OSD([sQuery(id+"F0.wireOp",EDGE,"E42.MirrorCS"),sQuery(id+"F0.wireOp",EDGE,"E60.MirrorCS"),sQuery(id+"F0.wireOp",EDGE,"E65.MirrorCS")])]});
            var Q26;
            Q26=makeQuery(id+"F1.opExtrude","SWEPT_EDGE",EDGE,{"disambiguationData":[OSD([sQuery(id+"F0.wireOp",EDGE,"E84.MirrorCS"),sQuery(id+"F0.wireOp",EDGE,"E86.MirrorCS"),sQuery(id+"F0.wireOp",EDGE,"E114.MirrorCS")])]});
            var Q27;
            Q27=makeQuery(id+"F1.opExtrude","SWEPT_EDGE",EDGE,{"disambiguationData":[OSD([sQuery(id+"F0.wireOp",EDGE,"E130.bottom"),sQuery(id+"F0.wireOp",EDGE,"E130.right")])]});
            var Q28;
            Q28=makeQuery(id+"F1.opExtrude","SWEPT_EDGE",EDGE,{"disambiguationData":[OSD([sQuery(id+"F0.wireOp",EDGE,"E130.top"),sQuery(id+"F0.wireOp",EDGE,"E130.right")])]});
            var Q29;
            Q29=makeQuery(id+"F1.opExtrude","SWEPT_EDGE",EDGE,{"disambiguationData":[OSD([sQuery(id+"F0.wireOp",EDGE,"E131.bottom"),sQuery(id+"F0.wireOp",EDGE,"E131.right")])]});
            var Q30;
            Q30=makeQuery(id+"F1.opExtrude","SWEPT_EDGE",EDGE,{"disambiguationData":[OSD([sQuery(id+"F0.wireOp",EDGE,"E131.top"),sQuery(id+"F0.wireOp",EDGE,"E131.right")])]});
            var Q31;
            Q31=makeQuery(id+"F1.opExtrude","SWEPT_EDGE",EDGE,{"disambiguationData":[OSD([sQuery(id+"F0.wireOp",EDGE,"E58.MirrorCS"),sQuery(id+"F0.wireOp",EDGE,"E65.MirrorCS")])]});
            var Q32;
            Q32=makeQuery(id+"F1.opExtrude","SWEPT_EDGE",EDGE,{"disambiguationData":[OSD([sQuery(id+"F0.wireOp",EDGE,"E84.MirrorCS"),sQuery(id+"F0.wireOp",EDGE,"E105.MirrorCS")])]});
            fillet(context, id + "F4", {"entities" : qUnion([Q0, Q1, Q2, Q3, Q4, Q5, Q6, Q7, Q8, Q9, Q10, Q11, Q12, Q13, Q14, Q15, Q16, Q17, Q18, Q19, Q20, Q21, Q22, Q23, Q24, Q25, Q26, Q27, Q28, Q29, Q30, Q31, Q32]), "radius" : 1 * mm, "tangentPropagation" : true, "allowEdgeOverflow" : false});
        }
    });
